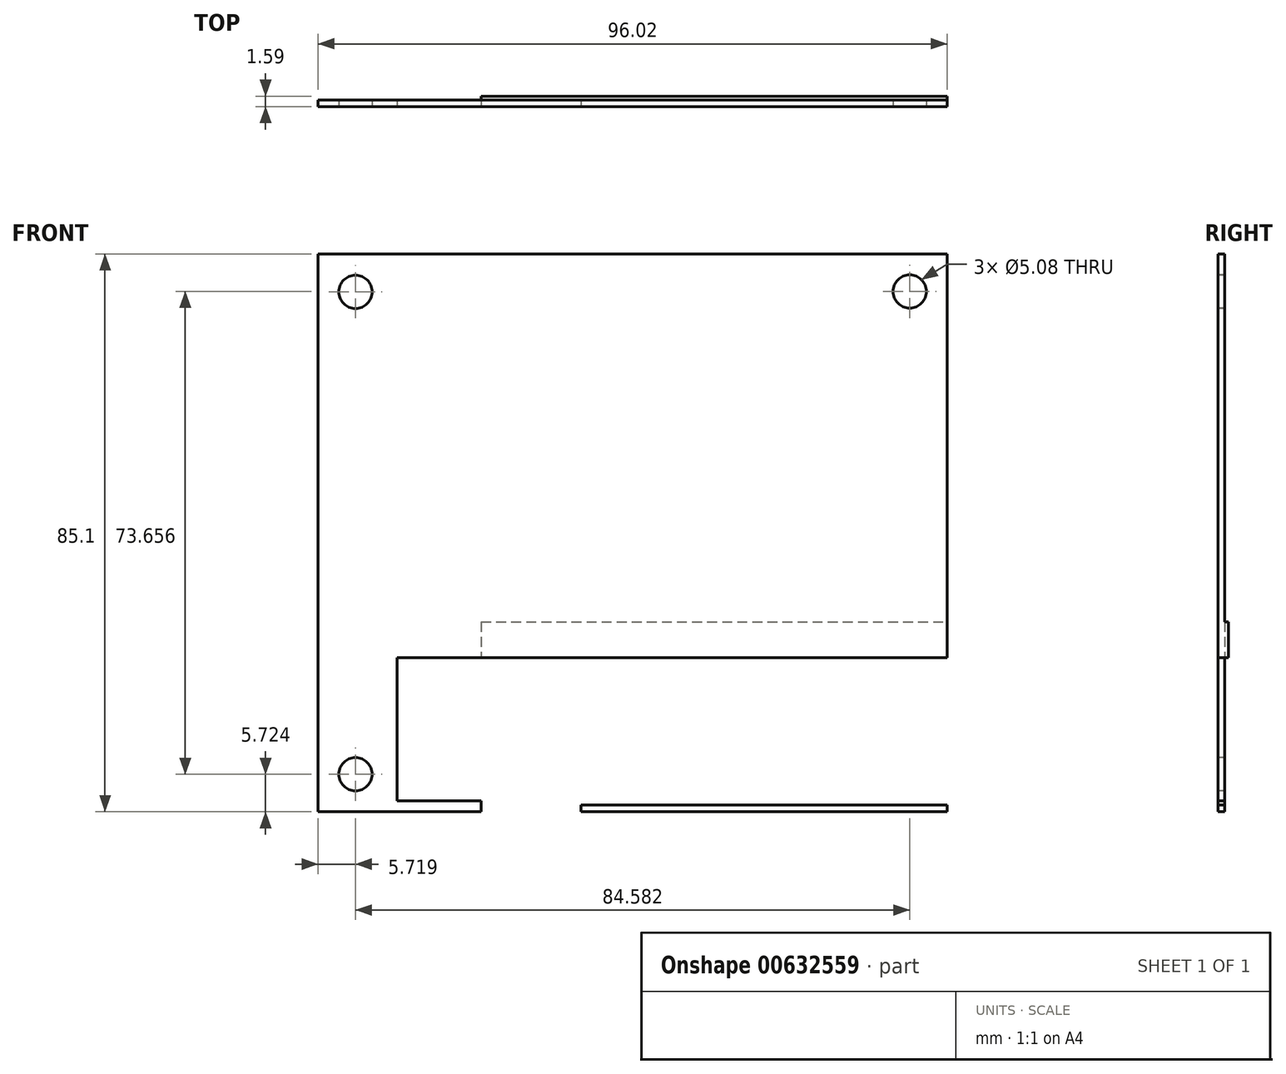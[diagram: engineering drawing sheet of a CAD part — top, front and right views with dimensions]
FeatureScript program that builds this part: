
annotation { "Feature Type Name" : "Feature", "Feature Type Description" : "" }
export const myFeature = defineFeature(function(context is Context, id is Id, definition is map)
    precondition{}
    {
        {
            var Q0;
            Q0=qCreatedBy(makeId("Front.planeOp"),FACE);
            var sketch = newSketch(context, id + "F0", { "sketchPlane" : qUnion([Q0])});
            skLineSegment(sketch, "E0.bottom", {"start": v(48, -42.55) * mm, "end": v(-48, -42.55) * mm});
            skLineSegment(sketch, "E0.top", {"start": v(48, 42.55) * mm, "end": v(-48, 42.55) * mm});
            skLineSegment(sketch, "E0.left", {"start": v(48, -42.55) * mm, "end": v(48, 42.55) * mm});
            skLineSegment(sketch, "E0.right", {"start": v(-48, -42.55) * mm, "end": v(-48, 42.55) * mm});
            skPoint(sketch, "E0.middle", {"position": v(0, 0) * mm});
            skSolve(sketch);
        }
        {
            var Q0;
            Q0 = qSketchRegion(id + "F0", true);
            extrude(context, id + "F1", {"entities" : qUnion([Q0]), "depth" : 1.02 * mm, "offsetDistance" : 25.4 * mm});
        }
        {
            var Q0;
            Q0=makeQuery(id+"F1.opExtrude","CAP_FACE",FACE,{"disambiguationData":[OSD([sQuery(id+"F0.wireOp",EDGE,"E0.bottom"),sQuery(id+"F0.wireOp",EDGE,"E0.top"),sQuery(id+"F0.wireOp",EDGE,"E0.left"),sQuery(id+"F0.wireOp",EDGE,"E0.right")])],"isStart":true});
            var sketch = newSketch(context, id + "F2", { "sketchPlane" : qUnion([Q0])});
            skPoint(sketch, "E1.middle", {"position": v(48, 26.46) * mm});
            skLineSegment(sketch, "E2.bottom", {"start": v(53, -17.4) * mm, "end": v(25.05, -17.4) * mm});
            skLineSegment(sketch, "E2.top", {"start": v(53, 41.01) * mm, "end": v(25.05, 41.01) * mm});
            skLineSegment(sketch, "E2.left", {"start": v(53, -17.4) * mm, "end": v(53, 41.01) * mm});
            skLineSegment(sketch, "E2.right", {"start": v(25.05, -17.4) * mm, "end": v(25.05, 41.01) * mm});
            skSolve(sketch);
        }
        {
            var Q0;
            {var subQ1=sQuery(id+"F2.wireOp",EDGE,"E2.top");Q0=makeQuery(id+"F2.imprint","IMPRINT",FACE,{"disambiguationData":[TD([[makeQuery(id+"F2.imprint","IMPRINT",EDGE,{"derivedFrom":subQ1}),1.0]])]});}
            var sketch = newSketch(context, id + "F3", { "sketchPlane" : qUnion([Q0])});
            skLineSegment(sketch, "E3.bottom", {"start": v(7.87, -41.53) * mm, "end": v(-51.82, -41.53) * mm});
            skLineSegment(sketch, "E3.top", {"start": v(7.87, -13.59) * mm, "end": v(-51.82, -13.59) * mm});
            skLineSegment(sketch, "E3.left", {"start": v(7.87, -41.53) * mm, "end": v(7.87, -13.59) * mm});
            skLineSegment(sketch, "E3.right", {"start": v(-51.82, -41.53) * mm, "end": v(-51.82, -13.59) * mm});
            skSolve(sketch);
        }
        {
            var Q0;
            Q0 = qSketchRegion(id + "F3", true);
            extrude(context, id + "F4", {"entities" : qUnion([Q0]), "operationType" : NewBodyOperationType.REMOVE, "oppositeDirection" : true, "depth" : 25.4 * mm, "offsetDistance" : 25.4 * mm});
        }
        {
            var Q0;
            Q0=makeQuery(id+"F1.opExtrude","CAP_FACE",FACE,{"disambiguationData":[OSD([sQuery(id+"F0.wireOp",EDGE,"E0.bottom"),sQuery(id+"F0.wireOp",EDGE,"E0.top"),sQuery(id+"F0.wireOp",EDGE,"E0.left"),sQuery(id+"F0.wireOp",EDGE,"E0.right")])],"isStart":false});
            var sketch = newSketch(context, id + "F5", { "sketchPlane" : qUnion([Q0])});
            skLineSegment(sketch, "E4.bottom", {"start": v(-7.87, -13.59) * mm, "end": v(-23.11, -13.59) * mm});
            skLineSegment(sketch, "E4.top", {"start": v(-7.87, -42.55) * mm, "end": v(-23.11, -42.55) * mm});
            skLineSegment(sketch, "E4.left", {"start": v(-7.87, -13.59) * mm, "end": v(-7.87, -42.55) * mm});
            skLineSegment(sketch, "E4.right", {"start": v(-23.11, -13.59) * mm, "end": v(-23.11, -42.55) * mm});
            skSolve(sketch);
        }
        {
            var Q0;
            Q0 = qSketchRegion(id + "F5", true);
            extrude(context, id + "F6", {"entities" : qUnion([Q0]), "operationType" : NewBodyOperationType.REMOVE, "oppositeDirection" : true, "depth" : 25.4 * mm, "offsetDistance" : 25.4 * mm});
        }
        {
            var Q0;
            Q0=makeQuery(id+"F1.opExtrude","CAP_FACE",FACE,{"disambiguationData":[OSD([sQuery(id+"F0.wireOp",EDGE,"E0.bottom"),sQuery(id+"F0.wireOp",EDGE,"E0.top"),sQuery(id+"F0.wireOp",EDGE,"E0.left"),sQuery(id+"F0.wireOp",EDGE,"E0.right")])],"isStart":false});
            var sketch = newSketch(context, id + "F7", { "sketchPlane" : qUnion([Q0])});
            skLineSegment(sketch, "E5.bottom", {"start": v(-23.11, -13.59) * mm, "end": v(48, -13.59) * mm});
            skLineSegment(sketch, "E5.top", {"start": v(-23.11, -19.01) * mm, "end": v(48, -19.01) * mm});
            skLineSegment(sketch, "E5.left", {"start": v(-23.11, -13.59) * mm, "end": v(-23.11, -19.01) * mm});
            skLineSegment(sketch, "E5.right", {"start": v(48, -13.59) * mm, "end": v(48, -19.01) * mm});
            skSolve(sketch);
        }
        {
            var Q0;
            Q0=makeQuery(id+"F7.imprint","IMPRINT",FACE,{"disambiguationData":[TD([[makeQuery(id+"F7.imprint","IMPRINT",EDGE,{"derivedFrom":sQuery(id+"F7.wireOp",EDGE,"E5.top")}),1.0]])]});
            extrude(context, id + "F8", {"entities" : qUnion([Q0]), "operationType" : NewBodyOperationType.ADD, "oppositeDirection" : true, "depth" : 1.59 * mm, "offsetDistance" : 25.4 * mm});
        }
        {
            var Q0;
            Q0=makeQuery(id+"F8.boolean.opBoolean","MERGE",FACE,{"derivedFrom":[makeQuery(id+"F1.opExtrude","CAP_FACE",FACE,{"disambiguationData":[OSD([sQuery(id+"F0.wireOp",EDGE,"E0.bottom"),sQuery(id+"F0.wireOp",EDGE,"E0.top"),sQuery(id+"F0.wireOp",EDGE,"E0.left"),sQuery(id+"F0.wireOp",EDGE,"E0.right")])],"isStart":false}),makeQuery(id+"F8.opExtrude","CAP_FACE",FACE,{"disambiguationData":[OSD([sQuery(id+"F7.wireOp",EDGE,"E5.bottom"),sQuery(id+"F7.wireOp",EDGE,"E5.top"),sQuery(id+"F7.wireOp",EDGE,"E5.left"),sQuery(id+"F7.wireOp",EDGE,"E5.right")])],"isStart":true})]});
            var sketch = newSketch(context, id + "F9", { "sketchPlane" : qUnion([Q0])});
            skLineSegment(sketch, "E6.bottom", {"start": v(-23.11, -19.01) * mm, "end": v(-35.96, -19.01) * mm});
            skLineSegment(sketch, "E6.top", {"start": v(-23.11, -40.9) * mm, "end": v(-35.96, -40.9) * mm});
            skLineSegment(sketch, "E6.left", {"start": v(-23.11, -19.01) * mm, "end": v(-23.11, -40.9) * mm});
            skLineSegment(sketch, "E6.right", {"start": v(-35.96, -19.01) * mm, "end": v(-35.96, -40.9) * mm});
            skSolve(sketch);
        }
        {
            var Q0;
            Q0 = qSketchRegion(id + "F9", true);
            extrude(context, id + "F10", {"entities" : qUnion([Q0]), "operationType" : NewBodyOperationType.REMOVE, "oppositeDirection" : true, "depth" : 3.17 * mm, "offsetDistance" : 25.4 * mm});
        }
        {
            var Q0;
            Q0=makeQuery(id+"F8.boolean.opBoolean","MERGE",FACE,{"derivedFrom":[makeQuery(id+"F1.opExtrude","CAP_FACE",FACE,{"disambiguationData":[OSD([sQuery(id+"F0.wireOp",EDGE,"E0.bottom"),sQuery(id+"F0.wireOp",EDGE,"E0.top"),sQuery(id+"F0.wireOp",EDGE,"E0.left"),sQuery(id+"F0.wireOp",EDGE,"E0.right")])],"isStart":false}),makeQuery(id+"F8.opExtrude","CAP_FACE",FACE,{"disambiguationData":[OSD([sQuery(id+"F7.wireOp",EDGE,"E5.bottom"),sQuery(id+"F7.wireOp",EDGE,"E5.top"),sQuery(id+"F7.wireOp",EDGE,"E5.left"),sQuery(id+"F7.wireOp",EDGE,"E5.right")])],"isStart":true})]});
            var sketch = newSketch(context, id + "F11", { "sketchPlane" : qUnion([Q0])});
            skPoint(sketch, "E7", {"position": v(-42.3, 36.79) * mm});
            skPoint(sketch, "E8", {"position": v(42.3, 36.83) * mm});
            skPoint(sketch, "E9", {"position": v(-42.3, -36.83) * mm});
            skSolve(sketch);
        }
        {
            var Q0;
            Q0=sQuery(id+"F11.wireOp",VERTEX,"E7");
            var Q1;
            Q1=sQuery(id+"F11.wireOp",VERTEX,"E9");
            var Q2;
            Q2=sQuery(id+"F11.wireOp",VERTEX,"E8");
            var Q3;
            Q3=makeQuery(id+"F1.opExtrude","SWEPT_BODY",BODY,{"disambiguationData":[OSD([sQuery(id+"F0.wireOp",EDGE,"E0.bottom"),sQuery(id+"F0.wireOp",EDGE,"E0.top"),sQuery(id+"F0.wireOp",EDGE,"E0.left"),sQuery(id+"F0.wireOp",EDGE,"E0.right")])]});
            hole(context, id + "F12", {"style" : HoleStyle.SIMPLE, "endStyle" : HoleEndStyle.THROUGH, "holeDiameter" : 5.08 * mm, "majorDiameter" : 6.35 * mm, "isTappedThrough" : true, "tappedDepth" : 12.7 * mm, "tapClearance" : 3, "locations" : qUnion([Q0, Q1, Q2]), "scope" : qUnion([Q3])});
        }
    });
